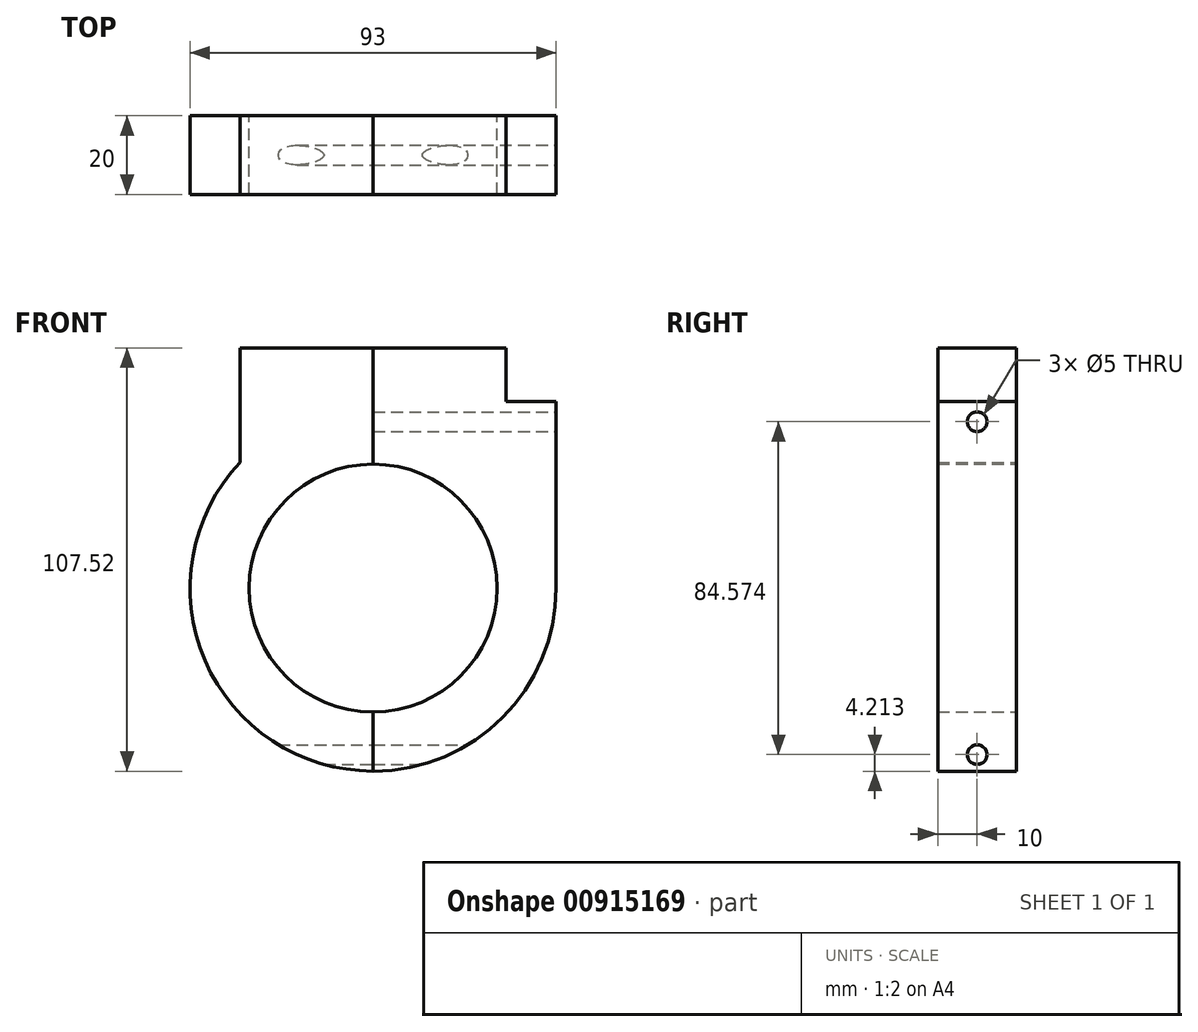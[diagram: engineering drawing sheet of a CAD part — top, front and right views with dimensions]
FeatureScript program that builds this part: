
annotation { "Feature Type Name" : "Feature", "Feature Type Description" : "" }
export const myFeature = defineFeature(function(context is Context, id is Id, definition is map)
    precondition{}
    {
        {
            var Q0;
            Q0=qCreatedBy(makeId("Front.planeOp"),FACE);
            var sketch = newSketch(context, id + "F0", { "sketchPlane" : qUnion([Q0])});
            skCircle(sketch, "E0", {"center": v(0, 0) * mm, "radius": 31.5 * mm});
            skCircle(sketch, "E1", {"center": v(0, 0) * mm, "radius": 46.5 * mm});
            skLineSegment(sketch, "E2", {"start": v(0, 46.5) * mm, "end": v(0, 31.5) * mm});
            skLineSegment(sketch, "E3", {"start": v(0, -31.5) * mm, "end": v(0, -46.5) * mm});
            skLineSegment(sketch, "E4.bottom", {"start": v(-33.76, 31.98) * mm, "end": v(33.76, 31.98) * mm});
            skLineSegment(sketch, "E4.top", {"start": v(-33.76, 61.02) * mm, "end": v(33.76, 61.02) * mm});
            skLineSegment(sketch, "E4.left", {"start": v(-33.76, 31.98) * mm, "end": v(-33.76, 61.02) * mm});
            skLineSegment(sketch, "E4.right", {"start": v(33.76, 31.98) * mm, "end": v(33.76, 61.02) * mm});
            skPoint(sketch, "E4.middle", {"position": v(0, 46.5) * mm});
            skLineSegment(sketch, "E5", {"start": v(46.5, 61.02) * mm, "end": v(46.5, -59.43) * mm, "construction": true});
            skLineSegment(sketch, "E6", {"start": v(46.5, 61.02) * mm, "end": v(33.76, 61.02) * mm, "construction": true});
            skPoint(sketch, "E7", {"position": v(46.5, 0) * mm});
            skLineSegment(sketch, "E8.bottom", {"start": v(46.5, 47.4) * mm, "end": v(-46.5, 47.4) * mm});
            skLineSegment(sketch, "E8.top", {"start": v(46.5, -47.4) * mm, "end": v(-46.5, -47.4) * mm});
            skLineSegment(sketch, "E8.left", {"start": v(46.5, 47.4) * mm, "end": v(46.5, -47.4) * mm});
            skLineSegment(sketch, "E8.right", {"start": v(-46.5, 47.4) * mm, "end": v(-46.5, -47.4) * mm});
            skLineSegment(sketch, "E9", {"start": v(0, 46.5) * mm, "end": v(0, 61.02) * mm});
            skSolve(sketch);
        }
        {
            var Q0;
            {var subQ0=sQuery(id+"F0.wireOp",EDGE,"E4.right");var subQ1=sQuery(id+"F0.wireOp",EDGE,"E4.top");var subQ2=makeQuery(id+"F0.imprint","INTERSECT",VERTEX,{"derivedFrom":[subQ1,subQ0]});Q0=makeQuery(id+"F0.imprint","IMPRINT",FACE,{"disambiguationData":[TD([[makeQuery(id+"F0.imprint","IMPRINT",EDGE,{"disambiguationData":[TD([[subQ2,1.0]])],"derivedFrom":subQ1}),-1.0]])]});}
            var Q1;
            {var subQ3=sQuery(id+"F0.wireOp",EDGE,"E4.right");var subQ5=sQuery(id+"F0.wireOp",EDGE,"E8.bottom");var subQ7=makeQuery(id+"F0.imprint","INTERSECT",VERTEX,{"derivedFrom":[subQ3,subQ5]});Q1=makeQuery(id+"F0.imprint","IMPRINT",FACE,{"disambiguationData":[TD([[makeQuery(id+"F0.imprint","IMPRINT",EDGE,{"disambiguationData":[TD([[subQ7,-1.0]])],"derivedFrom":subQ5}),1.0]])]});}
            var Q2;
            {var subQ0=sQuery(id+"F0.wireOp",EDGE,"E2");var subQ3=sQuery(id+"F0.wireOp",EDGE,"E4.bottom");var subQ5=makeQuery(id+"F0.imprint","INTERSECT",VERTEX,{"derivedFrom":[subQ0,subQ3]});Q2=makeQuery(id+"F0.imprint","IMPRINT",FACE,{"disambiguationData":[TD([[makeQuery(id+"F0.imprint","IMPRINT",EDGE,{"disambiguationData":[TD([[subQ5,1.0]])],"derivedFrom":subQ0}),1.0]])]});}
            var Q3;
            {var subQ5=sQuery(id+"F0.wireOp",EDGE,"E3");Q3=makeQuery(id+"F0.imprint","IMPRINT",FACE,{"disambiguationData":[TD([[makeQuery(id+"F0.imprint","IMPRINT",EDGE,{"derivedFrom":subQ5}),1.0]])]});}
            var Q4;
            {var subQ3=sQuery(id+"F0.wireOp",EDGE,"E8.left");var subQ5=sQuery(id+"F0.wireOp",EDGE,"E8.bottom");var subQ7=makeQuery(id+"F0.imprint","INTERSECT",VERTEX,{"derivedFrom":[subQ5,subQ3]});Q4=makeQuery(id+"F0.imprint","IMPRINT",FACE,{"disambiguationData":[TD([[makeQuery(id+"F0.imprint","IMPRINT",EDGE,{"disambiguationData":[TD([[subQ7,-1.0]])],"derivedFrom":subQ5}),1.0]])]});}
            extrude(context, id + "F1", {"entities" : qUnion([Q0, Q1, Q2, Q3, Q4]), "endBound" : BoundingType.SYMMETRIC, "depth" : 20 * mm, "offsetDistance" : 25 * mm});
        }
        {
            var Q0;
            Q0=makeQuery(id+"F1.opExtrude","SWEPT_FACE",FACE,{"disambiguationData":[OSD([sQuery(id+"F0.wireOp",EDGE,"E8.left")])]});
            var sketch = newSketch(context, id + "F2", { "sketchPlane" : qUnion([Q0])});
            skLineSegment(sketch, "E10", {"start": v(-10, -46.5) * mm, "end": v(-10, -47) * mm});
            skLineSegment(sketch, "E11.bottom", {"start": v(-10, -46.5) * mm, "end": v(10, -46.5) * mm});
            skLineSegment(sketch, "E11.top", {"start": v(-10, 47.4) * mm, "end": v(10, 47.4) * mm});
            skLineSegment(sketch, "E11.left", {"start": v(-10, -46.5) * mm, "end": v(-10, 47.4) * mm});
            skLineSegment(sketch, "E11.right", {"start": v(10, -46.5) * mm, "end": v(10, 47.4) * mm});
            skLineSegment(sketch, "E12", {"start": v(0, 47.4) * mm, "end": v(0, -46.5) * mm});
            skLineSegment(sketch, "E13", {"start": v(-10, 0) * mm, "end": v(10, 0) * mm});
            skPoint(sketch, "E14", {"position": v(0, 42.29) * mm});
            skPoint(sketch, "E15.MirrorP", {"position": v(0, -42.29) * mm});
            skSolve(sketch);
        }
        {
            var Q0;
            Q0=sQuery(id+"F2.wireOp",VERTEX,"E14");
            var Q1;
            Q1=makeQuery(id+"F1.opExtrude","SWEPT_BODY",BODY,{"disambiguationData":[OSD([sQuery(id+"F0.wireOp",EDGE,"E0"),sQuery(id+"F0.wireOp",EDGE,"E1"),sQuery(id+"F0.wireOp",EDGE,"E2"),sQuery(id+"F0.wireOp",EDGE,"E3"),sQuery(id+"F0.wireOp",EDGE,"E4.top"),sQuery(id+"F0.wireOp",EDGE,"E4.right"),sQuery(id+"F0.wireOp",EDGE,"E8.bottom"),sQuery(id+"F0.wireOp",EDGE,"E8.left"),sQuery(id+"F0.wireOp",EDGE,"E9")])]});
            hole(context, id + "F3", {"style" : HoleStyle.SIMPLE, "endStyle" : HoleEndStyle.THROUGH, "standardTappedOrClearance" : lookupTablePath({ "standard" : "ISO", "size" : "5", "type" : "Drilled" }), "standardBlindInLast" : lookupTablePath({ "standard" : "ISO", "size" : "5", "type" : "Drilled" }), "holeDiameter" : 5 * mm, "majorDiameter" : 5 * mm, "isTappedThrough" : true, "tappedDepth" : 12 * mm, "tapClearance" : 3, "startFromSketch" : true, "locations" : qUnion([Q0]), "scope" : qUnion([Q1])});
        }
        {
            var Q0;
            {var subQ0=sQuery(id+"F0.wireOp",EDGE,"E2");var subQ3=sQuery(id+"F0.wireOp",EDGE,"E4.bottom");var subQ5=makeQuery(id+"F0.imprint","INTERSECT",VERTEX,{"derivedFrom":[subQ0,subQ3]});Q0=makeQuery(id+"F0.imprint","IMPRINT",FACE,{"disambiguationData":[TD([[makeQuery(id+"F0.imprint","IMPRINT",EDGE,{"disambiguationData":[TD([[subQ5,1.0]])],"derivedFrom":subQ0}),-1.0]])]});}
            var Q1;
            {var subQ5=sQuery(id+"F0.wireOp",EDGE,"E3");Q1=makeQuery(id+"F0.imprint","IMPRINT",FACE,{"disambiguationData":[TD([[makeQuery(id+"F0.imprint","IMPRINT",EDGE,{"derivedFrom":subQ5}),-1.0]])]});}
            var Q2;
            {var subQ0=sQuery(id+"F0.wireOp",EDGE,"E4.left");var subQ1=sQuery(id+"F0.wireOp",EDGE,"E4.top");var subQ2=makeQuery(id+"F0.imprint","INTERSECT",VERTEX,{"derivedFrom":[subQ1,subQ0]});Q2=makeQuery(id+"F0.imprint","IMPRINT",FACE,{"disambiguationData":[TD([[makeQuery(id+"F0.imprint","IMPRINT",EDGE,{"disambiguationData":[TD([[subQ2,-1.0]])],"derivedFrom":subQ1}),-1.0]])]});}
            var Q3;
            {var subQ3=sQuery(id+"F0.wireOp",EDGE,"E4.left");var subQ5=sQuery(id+"F0.wireOp",EDGE,"E8.bottom");var subQ6=makeQuery(id+"F0.imprint","INTERSECT",VERTEX,{"derivedFrom":[subQ3,subQ5]});Q3=makeQuery(id+"F0.imprint","IMPRINT",FACE,{"disambiguationData":[TD([[makeQuery(id+"F0.imprint","IMPRINT",EDGE,{"disambiguationData":[TD([[subQ6,1.0]])],"derivedFrom":subQ5}),1.0]])]});}
            extrude(context, id + "F4", {"entities" : qUnion([Q0, Q1, Q2, Q3]), "endBound" : BoundingType.SYMMETRIC, "depth" : 20 * mm, "offsetDistance" : 25 * mm});
        }
        {
            var Q0;
            Q0=sQuery(id+"F2.wireOp",VERTEX,"E15.MirrorP");
            var Q1;
            Q1=makeQuery(id+"F1.opExtrude","SWEPT_BODY",BODY,{"disambiguationData":[OSD([sQuery(id+"F0.wireOp",EDGE,"E0"),sQuery(id+"F0.wireOp",EDGE,"E1"),sQuery(id+"F0.wireOp",EDGE,"E2"),sQuery(id+"F0.wireOp",EDGE,"E3"),sQuery(id+"F0.wireOp",EDGE,"E4.top"),sQuery(id+"F0.wireOp",EDGE,"E4.right"),sQuery(id+"F0.wireOp",EDGE,"E8.bottom"),sQuery(id+"F0.wireOp",EDGE,"E8.left"),sQuery(id+"F0.wireOp",EDGE,"E9")])]});
            var Q2;
            Q2=makeQuery(id+"F4.opExtrude","SWEPT_BODY",BODY,{"disambiguationData":[OSD([sQuery(id+"F0.wireOp",EDGE,"E0"),sQuery(id+"F0.wireOp",EDGE,"E1"),sQuery(id+"F0.wireOp",EDGE,"E2"),sQuery(id+"F0.wireOp",EDGE,"E3"),sQuery(id+"F0.wireOp",EDGE,"E4.top"),sQuery(id+"F0.wireOp",EDGE,"E4.left"),sQuery(id+"F0.wireOp",EDGE,"E9")])]});
            hole(context, id + "F5", {"style" : HoleStyle.SIMPLE, "endStyle" : HoleEndStyle.THROUGH, "standardTappedOrClearance" : lookupTablePath({ "standard" : "ISO", "size" : "5", "type" : "Drilled" }), "standardBlindInLast" : lookupTablePath({ "standard" : "ISO", "size" : "5", "type" : "Drilled" }), "holeDiameter" : 5 * mm, "majorDiameter" : 5 * mm, "isTappedThrough" : true, "tappedDepth" : 12 * mm, "tapClearance" : 3, "startFromSketch" : true, "locations" : qUnion([Q0]), "scope" : qUnion([Q1, Q2])});
        }
    });
